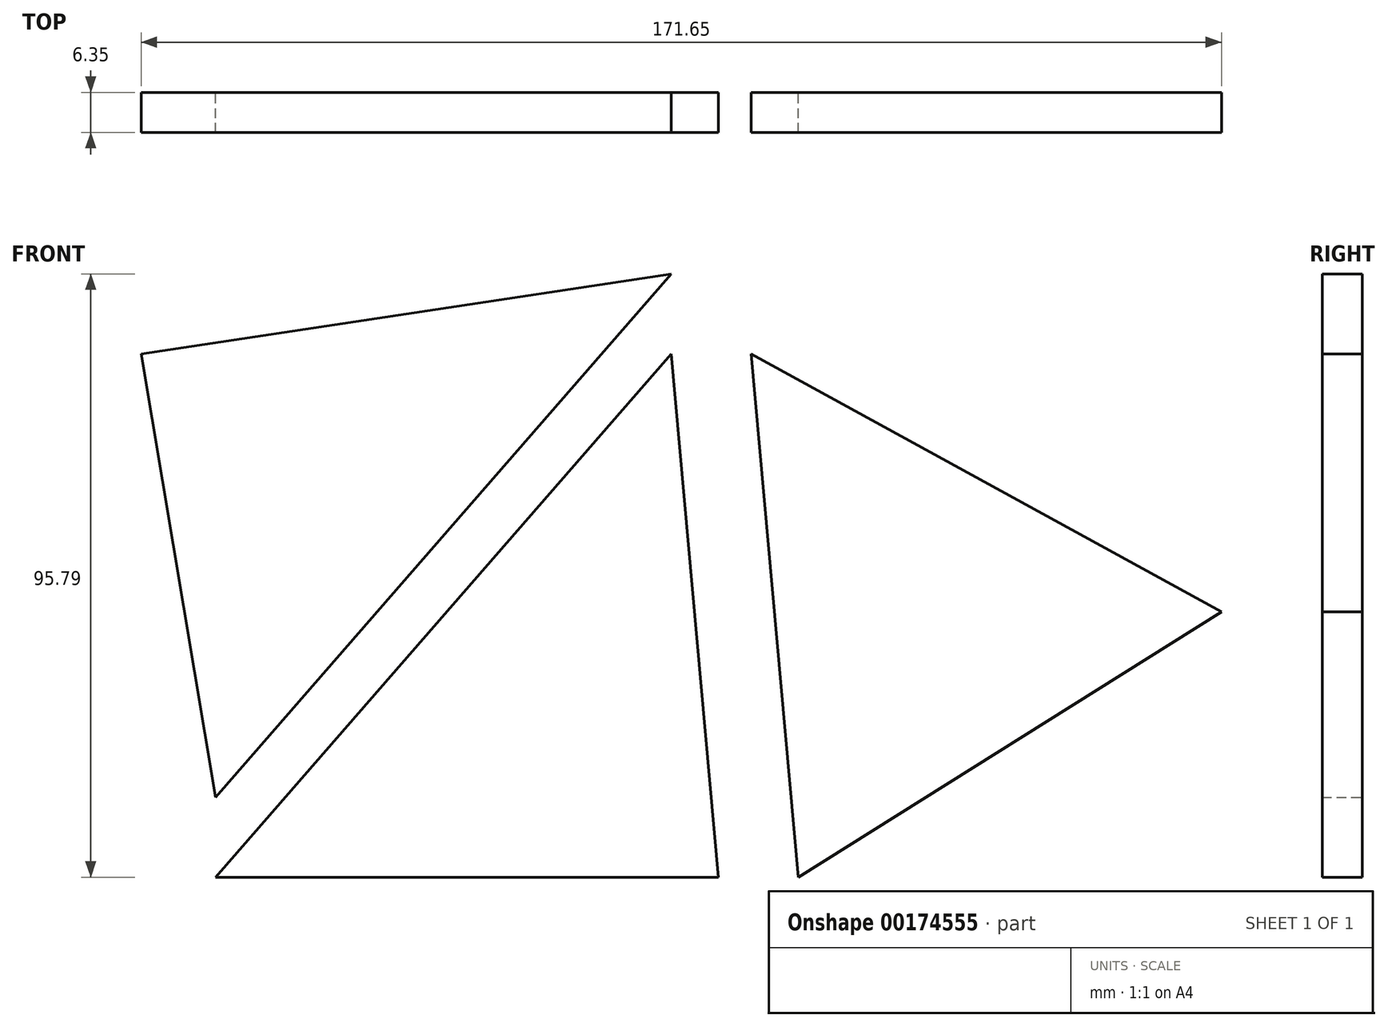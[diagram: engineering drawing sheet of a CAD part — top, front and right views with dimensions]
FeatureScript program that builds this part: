
annotation { "Feature Type Name" : "Feature", "Feature Type Description" : "" }
export const myFeature = defineFeature(function(context is Context, id is Id, definition is map)
    precondition{}
    {
        {
            var Q0;
            Q0=qCreatedBy(makeId("Front.planeOp"),FACE);
            var sketch = newSketch(context, id + "F0", { "sketchPlane" : qUnion([Q0])});
            skLineSegment(sketch, "E0", {"start": v(-84.24, 0) * mm, "end": v(0, 12.7) * mm});
            skLineSegment(sketch, "E1", {"start": v(0, 12.7) * mm, "end": v(-72.4, -70.39) * mm});
            skLineSegment(sketch, "E2", {"start": v(-72.4, -70.39) * mm, "end": v(-84.24, 0) * mm});
            skLineSegment(sketch, "E3", {"start": v(0, 0) * mm, "end": v(-72.4, -83.09) * mm});
            skLineSegment(sketch, "E4", {"start": v(-72.4, -83.09) * mm, "end": v(7.44, -83.09) * mm});
            skLineSegment(sketch, "E5", {"start": v(7.44, -83.09) * mm, "end": v(0, 0) * mm});
            skLineSegment(sketch, "E6", {"start": v(12.7, 0) * mm, "end": v(20.14, -83.09) * mm});
            skLineSegment(sketch, "E7", {"start": v(20.14, -83.09) * mm, "end": v(87.4, -40.94) * mm});
            skLineSegment(sketch, "E8", {"start": v(87.4, -40.94) * mm, "end": v(12.7, 0) * mm});
            skLineSegment(sketch, "E9", {"start": v(0, 12.7) * mm, "end": v(0, 0) * mm, "construction": true});
            skLineSegment(sketch, "E10", {"start": v(12.7, 0) * mm, "end": v(0, 0) * mm, "construction": true});
            skSolve(sketch);
        }
        {
            var Q0;
            Q0=qCreatedBy(makeId("Front.planeOp"),FACE);
            var sketch = newSketch(context, id + "F1", { "sketchPlane" : qUnion([Q0])});
            skLineSegment(sketch, "E11.0.0", {"start": v(0, 12.7) * mm, "end": v(-84.24, 0) * mm});
            skLineSegment(sketch, "E11.0.1", {"start": v(-84.24, 0) * mm, "end": v(-72.4, -70.39) * mm});
            skLineSegment(sketch, "E11.0.2", {"start": v(-72.4, -70.39) * mm, "end": v(0, 12.7) * mm});
            skLineSegment(sketch, "E12.0.0", {"start": v(7.44, -83.09) * mm, "end": v(0, 0) * mm});
            skLineSegment(sketch, "E12.0.1", {"start": v(0, 0) * mm, "end": v(-72.4, -83.09) * mm});
            skLineSegment(sketch, "E12.0.2", {"start": v(-72.4, -83.09) * mm, "end": v(7.44, -83.09) * mm});
            skLineSegment(sketch, "E13.0.0", {"start": v(87.4, -40.94) * mm, "end": v(12.7, 0) * mm});
            skLineSegment(sketch, "E13.0.1", {"start": v(12.7, 0) * mm, "end": v(20.14, -83.09) * mm});
            skLineSegment(sketch, "E13.0.2", {"start": v(20.14, -83.09) * mm, "end": v(87.4, -40.94) * mm});
            skSolve(sketch);
        }
        {
            var Q0;
            Q0 = qSketchRegion(id + "F1", true);
            extrude(context, id + "F2", {"entities" : qUnion([Q0]), "depth" : 6.35 * mm});
        }
    });
